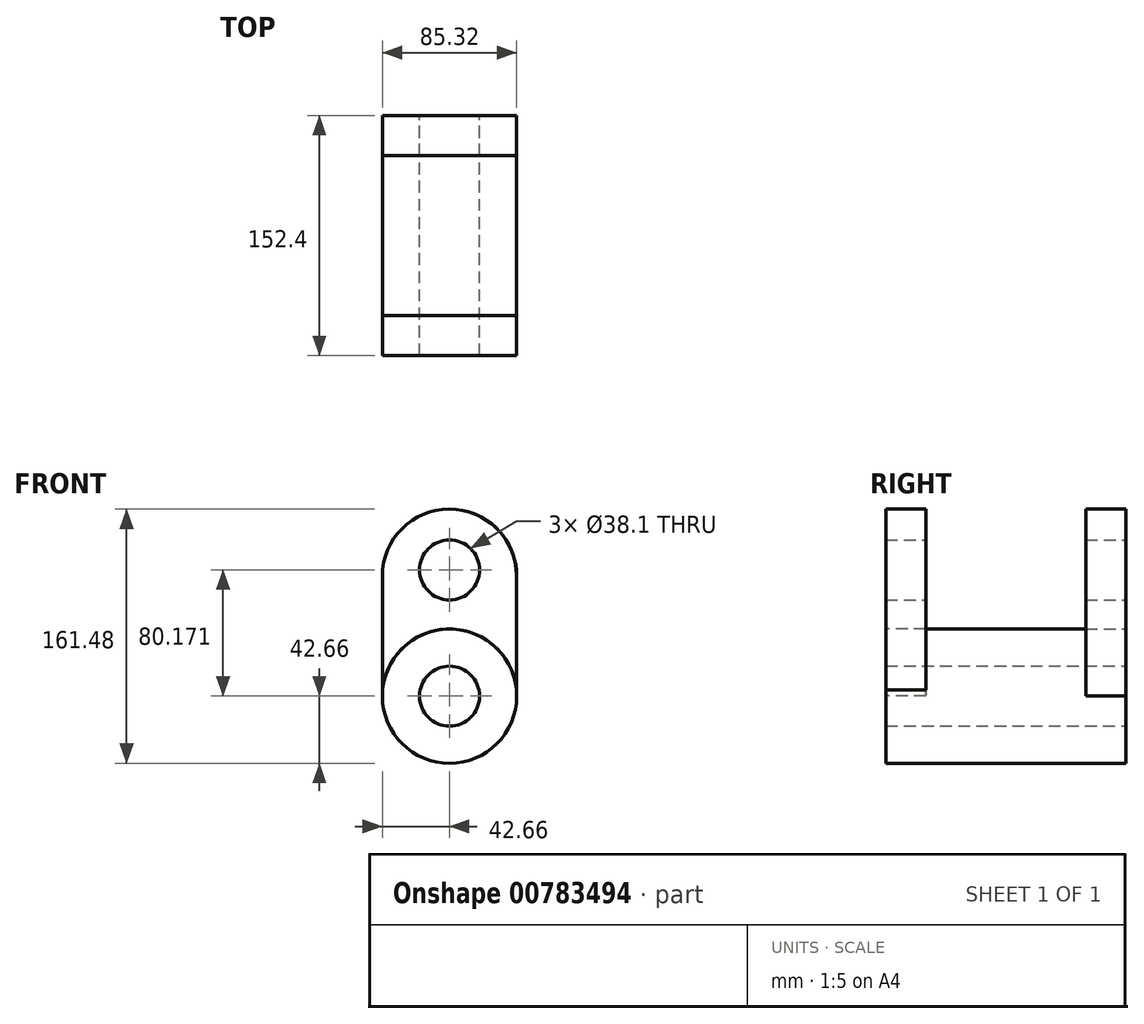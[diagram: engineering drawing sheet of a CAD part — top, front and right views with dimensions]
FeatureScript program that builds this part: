
annotation { "Feature Type Name" : "Feature", "Feature Type Description" : "" }
export const myFeature = defineFeature(function(context is Context, id is Id, definition is map)
    precondition{}
    {
        {
            var Q0;
            Q0=qCreatedBy(makeId("Front.planeOp"),FACE);
            var sketch = newSketch(context, id + "F0", { "sketchPlane" : qUnion([Q0])});
            skCircle(sketch, "E0", {"center": v(0, 0) * mm, "radius": 42.66 * mm});
            skLineSegment(sketch, "E1", {"start": v(-42.66, 0) * mm, "end": v(-42.66, 75.83) * mm});
            skLineSegment(sketch, "E2", {"start": v(42.66, 0) * mm, "end": v(42.66, 76.51) * mm});
            skArc(sketch, "E3", {"start": v(42.66, 76.51) * mm, "mid": v(-0.34, 119.18) * mm, "end": v(-42.66, 75.83) * mm});
            skSolve(sketch);
        }
        {
            var Q0;
            {var subQ0=sQuery(id+"F0.wireOp",EDGE,"E0");var subQ1=makeQuery(id+"F0.imprint","INTERSECT",VERTEX,{"derivedFrom":[subQ0,sQuery(id+"F0.wireOp",EDGE,"E1")]});Q0=makeQuery(id+"F0.imprint","IMPRINT",FACE,{"disambiguationData":[TD([[makeQuery(id+"F0.imprint","IMPRINT",EDGE,{"disambiguationData":[TD([[subQ1,1.0]])],"derivedFrom":subQ0}),1.0]])]});}
            extrude(context, id + "F1", {"entities" : qUnion([Q0]), "depth" : 152.4 * mm, "offsetDistance" : 25.4 * mm});
        }
        {
            var Q0;
            Q0=makeQuery(id+"F1.opExtrude","CAP_FACE",FACE,{"disambiguationData":[OSD([sQuery(id+"F0.wireOp",EDGE,"E0")])],"isStart":true});
            var sketch = newSketch(context, id + "F2", { "sketchPlane" : qUnion([Q0])});
            skLineSegment(sketch, "E4", {"start": v(-42.66, 0) * mm, "end": v(-42.66, 76.13) * mm});
            skLineSegment(sketch, "E5", {"start": v(42.66, 0) * mm, "end": v(42.66, 76.13) * mm});
            skArc(sketch, "E6", {"start": v(42.66, 76.13) * mm, "mid": v(0, 118.8) * mm, "end": v(-42.66, 76.13) * mm});
            skSolve(sketch);
        }
        {
            var Q0;
            {var subQ0=sQuery(id+"F2.wireOp",EDGE,"E4");Q0=makeQuery(id+"F2.imprint","IMPRINT",FACE,{"disambiguationData":[TD([[makeQuery(id+"F2.imprint","IMPRINT",EDGE,{"derivedFrom":subQ0}),-1.0]])]});}
            extrude(context, id + "F3", {"entities" : qUnion([Q0]), "oppositeDirection" : true, "depth" : 25.4 * mm, "offsetDistance" : 25.4 * mm});
        }
        {
            var Q0;
            Q0=makeQuery(id+"F1.opExtrude","CAP_FACE",FACE,{"disambiguationData":[OSD([sQuery(id+"F0.wireOp",EDGE,"E0")])],"isStart":false});
            var sketch = newSketch(context, id + "F4", { "sketchPlane" : qUnion([Q0])});
            skLineSegment(sketch, "E7", {"start": v(-42.66, 0) * mm, "end": v(-42.66, 76.25) * mm});
            skLineSegment(sketch, "E8", {"start": v(42.48, 76.5) * mm, "end": v(42.48, 3.93) * mm});
            skArc(sketch, "E9", {"start": v(42.48, 76.5) * mm, "mid": v(-0.22, 118.82) * mm, "end": v(-42.66, 76.25) * mm});
            skSolve(sketch);
        }
        {
            var Q0;
            {var subQ0=sQuery(id+"F4.wireOp",EDGE,"E7");Q0=makeQuery(id+"F4.imprint","IMPRINT",FACE,{"disambiguationData":[TD([[makeQuery(id+"F4.imprint","IMPRINT",EDGE,{"derivedFrom":subQ0}),-1.0]])]});}
            extrude(context, id + "F5", {"entities" : qUnion([Q0]), "oppositeDirection" : true, "depth" : 25.4 * mm, "offsetDistance" : 25.4 * mm});
        }
        {
            var Q0;
            Q0=qCreatedBy(makeId("Front.planeOp"),FACE);
            var sketch = newSketch(context, id + "F6", { "sketchPlane" : qUnion([Q0])});
            skPoint(sketch, "E10", {"position": v(0, 80.17) * mm});
            skPoint(sketch, "E11", {"position": v(0, 0) * mm});
            skSolve(sketch);
        }
        {
            var Q0;
            Q0=sQuery(id+"F6.wireOp",VERTEX,"E10");
            var Q1;
            Q1=sQuery(id+"F6.wireOp",VERTEX,"E11");
            var Q2;
            Q2=makeQuery(id+"F3.opExtrude","SWEPT_BODY",BODY,{"disambiguationData":[OSD([sQuery(id+"F0.wireOp",EDGE,"E0"),sQuery(id+"F2.wireOp",EDGE,"E4"),sQuery(id+"F2.wireOp",EDGE,"E5"),sQuery(id+"F2.wireOp",EDGE,"E6")])]});
            var Q3;
            Q3=makeQuery(id+"F5.opExtrude","SWEPT_BODY",BODY,{"disambiguationData":[OSD([sQuery(id+"F0.wireOp",EDGE,"E0"),sQuery(id+"F4.wireOp",EDGE,"E7"),sQuery(id+"F4.wireOp",EDGE,"E8"),sQuery(id+"F4.wireOp",EDGE,"E9")])]});
            var Q4;
            Q4=makeQuery(id+"F1.opExtrude","SWEPT_BODY",BODY,{"disambiguationData":[OSD([sQuery(id+"F0.wireOp",EDGE,"E0")])]});
            hole(context, id + "F7", {"style" : HoleStyle.SIMPLE, "endStyle" : HoleEndStyle.THROUGH, "oppositeDirection" : true, "holeDiameter" : 38.1 * mm, "majorDiameter" : 6.35 * mm, "isTappedThrough" : true, "tappedDepth" : 12.7 * mm, "tapClearance" : 3, "locations" : qUnion([Q0, Q1]), "scope" : qUnion([Q2, Q3, Q4])});
        }
    });
